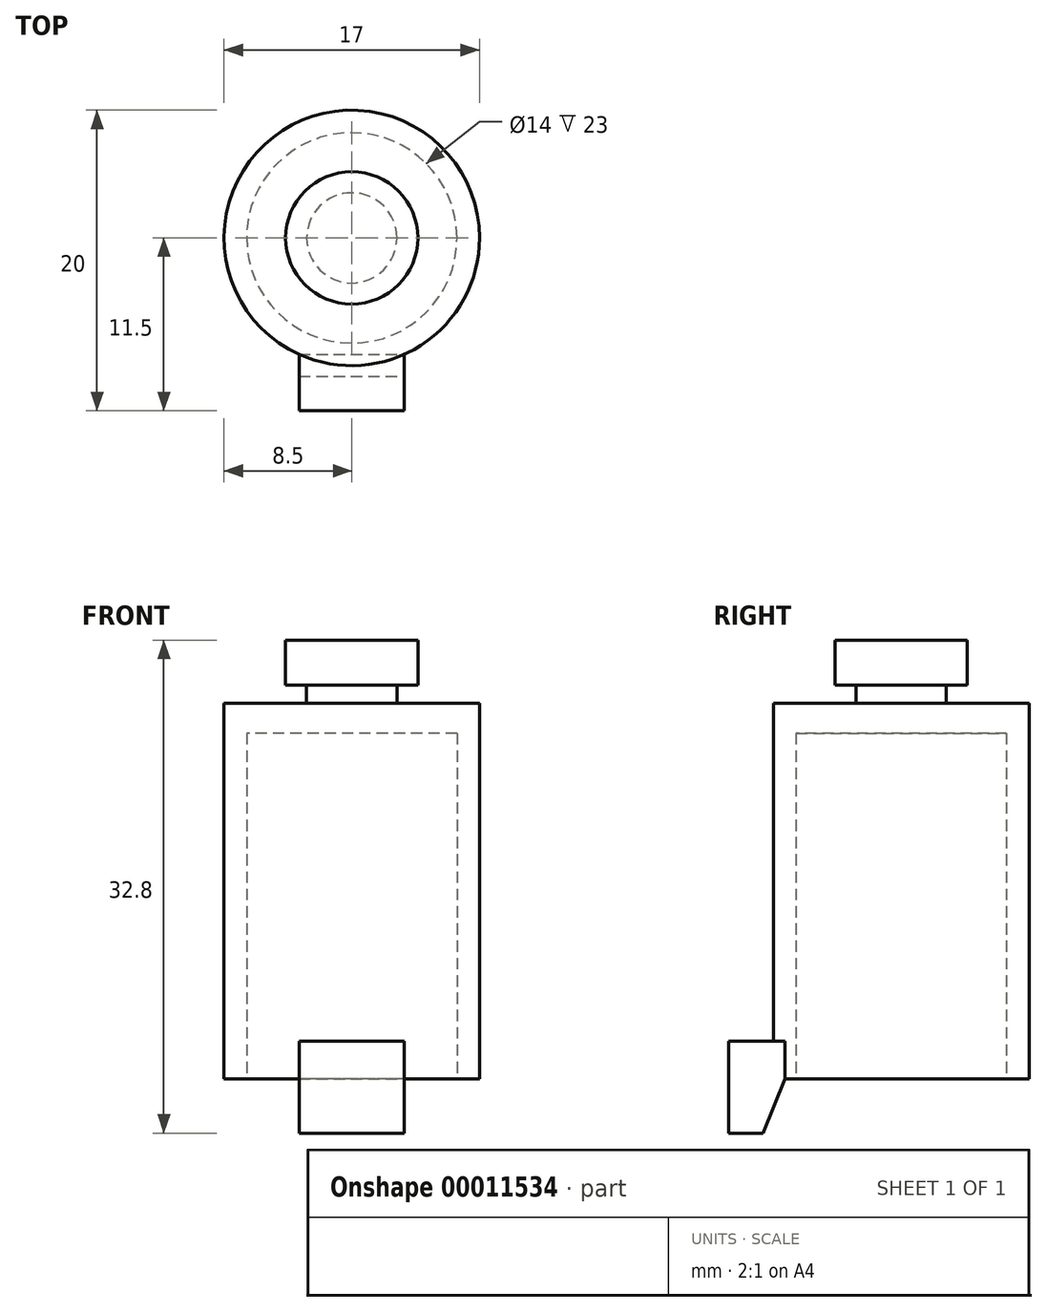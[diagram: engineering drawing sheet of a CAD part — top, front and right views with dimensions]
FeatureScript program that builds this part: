
annotation { "Feature Type Name" : "Feature", "Feature Type Description" : "" }
export const myFeature = defineFeature(function(context is Context, id is Id, definition is map)
    precondition{}
    {
        {
            var Q0;
            Q0=qCreatedBy(makeId("Top.planeOp"),FACE);
            var sketch = newSketch(context, id + "F0", { "sketchPlane" : qUnion([Q0])});
            skCircle(sketch, "E0", {"center": v(0, 0) * mm, "radius": 8.5 * mm});
            skCircle(sketch, "E1", {"center": v(0, 0) * mm, "radius": 7 * mm});
            skSolve(sketch);
        }
        {
            var Q0;
            Q0=makeQuery(id+"F0.imprint","IMPRINT",FACE,{"disambiguationData":[TD([[makeQuery(id+"F0.imprint","IMPRINT",EDGE,{"derivedFrom":sQuery(id+"F0.wireOp",EDGE,"E0")}),1.0]])]});
            extrude(context, id + "F1", {"entities" : qUnion([Q0]), "depth" : 25 * mm});
        }
        {
            var Q0;
            Q0=makeQuery(id+"F1.opExtrude","CAP_FACE",FACE,{"disambiguationData":[OSD([sQuery(id+"F0.wireOp",EDGE,"E0"),sQuery(id+"F0.wireOp",EDGE,"E1")])],"isStart":false});
            var sketch = newSketch(context, id + "F2", { "sketchPlane" : qUnion([Q0])});
            skCircle(sketch, "E2.0", {"center": v(0, 0) * mm, "radius": 8.5 * mm});
            skSolve(sketch);
        }
        {
            var Q0;
            Q0=makeQuery(id+"F2.imprint","IMPRINT",FACE,{"disambiguationData":[TD([[makeQuery(id+"F2.imprint","IMPRINT",EDGE,{"derivedFrom":sQuery(id+"F2.wireOp",EDGE,"E2.0")}),1.0]])]});
            var Q1;
            Q1=makeQuery(id+"F2.imprint","IMPRINT",FACE,{"disambiguationData":[TD([[makeQuery(id+"F2.imprint","IMPRINT",EDGE,{"derivedFrom":makeQuery(id+"F1.opExtrude","CAP_EDGE",EDGE,{"disambiguationData":[OSD([sQuery(id+"F0.wireOp",EDGE,"E1")])],"isStart":false})}),1.0]])]});
            extrude(context, id + "F3", {"entities" : qUnion([Q0, Q1]), "operationType" : NewBodyOperationType.ADD, "oppositeDirection" : true, "depth" : 2 * mm});
        }
        {
            var Q0;
            Q0=makeQuery(id+"F3.boolean.opBoolean","MERGE",FACE,{"derivedFrom":[makeQuery(id+"F1.opExtrude","CAP_FACE",FACE,{"disambiguationData":[OSD([sQuery(id+"F0.wireOp",EDGE,"E0"),sQuery(id+"F0.wireOp",EDGE,"E1")])],"isStart":false}),makeQuery(id+"F3.opExtrude","CAP_FACE",FACE,{"disambiguationData":[OSD([sQuery(id+"F2.wireOp",EDGE,"E2.0")])],"isStart":true})]});
            var sketch = newSketch(context, id + "F4", { "sketchPlane" : qUnion([Q0])});
            skCircle(sketch, "E3", {"center": v(0, 0) * mm, "radius": 3 * mm});
            skSolve(sketch);
        }
        {
            var Q0;
            Q0=makeQuery(id+"F4.imprint","IMPRINT",FACE,{"disambiguationData":[TD([[makeQuery(id+"F4.imprint","IMPRINT",EDGE,{"derivedFrom":sQuery(id+"F4.wireOp",EDGE,"E3")}),1.0]])]});
            extrude(context, id + "F5", {"entities" : qUnion([Q0]), "operationType" : NewBodyOperationType.ADD, "depth" : 1.2 * mm});
        }
        {
            var Q0;
            Q0=makeQuery(id+"F5.opExtrude","CAP_FACE",FACE,{"disambiguationData":[OSD([sQuery(id+"F4.wireOp",EDGE,"E3")])],"isStart":false});
            var sketch = newSketch(context, id + "F6", { "sketchPlane" : qUnion([Q0])});
            skCircle(sketch, "E4", {"center": v(0, 0) * mm, "radius": 4.4 * mm});
            skSolve(sketch);
        }
        {
            var Q0;
            Q0=makeQuery(id+"F6.imprint","IMPRINT",FACE,{"disambiguationData":[TD([[makeQuery(id+"F6.imprint","IMPRINT",EDGE,{"derivedFrom":sQuery(id+"F6.wireOp",EDGE,"E4")}),1.0]])]});
            var Q1;
            Q1=makeQuery(id+"F6.imprint","IMPRINT",FACE,{"disambiguationData":[TD([[makeQuery(id+"F6.imprint","IMPRINT",EDGE,{"derivedFrom":makeQuery(id+"F5.opExtrude","CAP_EDGE",EDGE,{"disambiguationData":[OSD([sQuery(id+"F4.wireOp",EDGE,"E3")])],"isStart":false})}),1.0]])]});
            extrude(context, id + "F7", {"entities" : qUnion([Q0, Q1]), "operationType" : NewBodyOperationType.ADD, "depth" : 3 * mm});
        }
        {
            var Q0;
            Q0=qCreatedBy(makeId("Top.planeOp"),FACE);
            var sketch = newSketch(context, id + "F8", { "sketchPlane" : qUnion([Q0])});
            skCircle(sketch, "E5.0", {"center": v(0, 0) * mm, "radius": 8.5 * mm});
            skLineSegment(sketch, "E6", {"start": v(-3.5, -7.75) * mm, "end": v(-3.5, -11.5) * mm});
            skLineSegment(sketch, "E7", {"start": v(-3.5, -11.5) * mm, "end": v(3.5, -11.5) * mm});
            skLineSegment(sketch, "E8", {"start": v(3.5, -11.5) * mm, "end": v(3.5, -7.75) * mm});
            skSolve(sketch);
        }
        {
            var Q0;
            {var subQ1=sQuery(id+"F8.wireOp",EDGE,"E6");Q0=makeQuery(id+"F8.imprint","IMPRINT",FACE,{"disambiguationData":[TD([[makeQuery(id+"F8.imprint","IMPRINT",EDGE,{"derivedFrom":subQ1}),1.0]])]});}
            extrude(context, id + "F9", {"entities" : qUnion([Q0]), "operationType" : NewBodyOperationType.ADD, "depth" : 2.5 * mm});
        }
        {
            var Q0;
            Q0=makeQuery(id+"F9.boolean.opBoolean","MERGE",FACE,{"derivedFrom":[makeQuery(id+"F1.opExtrude","CAP_FACE",FACE,{"disambiguationData":[OSD([sQuery(id+"F0.wireOp",EDGE,"E0"),sQuery(id+"F0.wireOp",EDGE,"E1")])],"isStart":true}),makeQuery(id+"F9.opExtrude","CAP_FACE",FACE,{"disambiguationData":[OSD([sQuery(id+"F8.wireOp",EDGE,"E5.0"),sQuery(id+"F8.wireOp",EDGE,"E6"),sQuery(id+"F8.wireOp",EDGE,"E7"),sQuery(id+"F8.wireOp",EDGE,"E8")])],"isStart":true})]});
            var sketch = newSketch(context, id + "F10", { "sketchPlane" : qUnion([Q0])});
            skCircle(sketch, "E9", {"center": v(0, 0) * mm, "radius": 8.5 * mm});
            skLineSegment(sketch, "E10.0", {"start": v(-3.5, 7.75) * mm, "end": v(-3.5, 11.5) * mm});
            skLineSegment(sketch, "E11.0", {"start": v(-3.5, 11.5) * mm, "end": v(3.5, 11.5) * mm});
            skLineSegment(sketch, "E12.0", {"start": v(3.5, 11.5) * mm, "end": v(3.5, 7.75) * mm});
            skSolve(sketch);
        }
        {
            var Q0;
            Q0=makeQuery(id+"F10.imprint","IMPRINT",FACE,{"disambiguationData":[TD([[makeQuery(id+"F10.imprint","IMPRINT",EDGE,{"disambiguationData":[OD(0.0)],"derivedFrom":sQuery(id+"F10.wireOp",EDGE,"E9")}),-1.0]])]});
            extrude(context, id + "F11", {"entities" : qUnion([Q0]), "operationType" : NewBodyOperationType.ADD, "depth" : 3.6 * mm});
        }
        {
            var Q0;
            Q0=makeQuery(id+"F11.boolean.opBoolean","MERGE",FACE,{"derivedFrom":[makeQuery(id+"F9.opExtrude","SWEPT_FACE",FACE,{"disambiguationData":[OSD([sQuery(id+"F8.wireOp",EDGE,"E8")])]}),makeQuery(id+"F11.opExtrude","SWEPT_FACE",FACE,{"disambiguationData":[OSD([sQuery(id+"F10.wireOp",EDGE,"E12.0")])]})]});
            var sketch = newSketch(context, id + "F12", { "sketchPlane" : qUnion([Q0])});
            skLineSegment(sketch, "E13", {"start": v(-7.75, 0) * mm, "end": v(-9.2, -3.6) * mm});
            skLineSegment(sketch, "E14", {"start": v(-9.2, -3.6) * mm, "end": v(-7.75, -3.6) * mm});
            skLineSegment(sketch, "E15", {"start": v(-7.75, -3.6) * mm, "end": v(-7.75, 0) * mm});
            skSolve(sketch);
        }
        {
            var Q0;
            Q0=makeQuery(id+"F12.imprint","IMPRINT",FACE,{"disambiguationData":[TD([[makeQuery(id+"F12.imprint","IMPRINT",EDGE,{"derivedFrom":sQuery(id+"F12.wireOp",EDGE,"E13")}),1.0]])]});
            extrude(context, id + "F13", {"entities" : qUnion([Q0]), "operationType" : NewBodyOperationType.REMOVE, "endBound" : BoundingType.THROUGH_ALL, "oppositeDirection" : true, "depth" : 25 * mm});
        }
        {
            var Q0;
            Q0=makeQuery(id+"F13.boolean.opBoolean","COPY",FACE,{"derivedFrom":makeQuery(id+"F13.opExtrude","SWEPT_FACE",FACE,{"disambiguationData":[OSD([sQuery(id+"F12.wireOp",EDGE,"E13")])]})});
            var sketch = newSketch(context, id + "F14", { "sketchPlane" : qUnion([Q0])});
            skLineSegment(sketch, "E16", {"start": v(3.5, -2.9) * mm, "end": v(-3.5, -2.9) * mm});
            skEllipticalArc(sketch, "E17.0", {});
            const initialGuessF14  = {"E17.0": [0, 0.017782341645010486, 0, 1, 0.02269665689378765, 0.0085, 2.717202944996607, 3.5659823621829787]};
            skSetInitialGuess(sketch, initialGuessF14);
            skSolve(sketch);
        }
        {
            var Q0;
            Q0=makeQuery(id+"F14.imprint","IMPRINT",FACE,{"disambiguationData":[TD([[makeQuery(id+"F14.imprint","IMPRINT",EDGE,{"derivedFrom":sQuery(id+"F14.wireOp",EDGE,"E16")}),1.0]])]});
            extrude(context, id + "F15", {"entities" : qUnion([Q0]), "operationType" : NewBodyOperationType.ADD, "oppositeDirection" : true, "depth" : 3 * mm});
        }
    });
